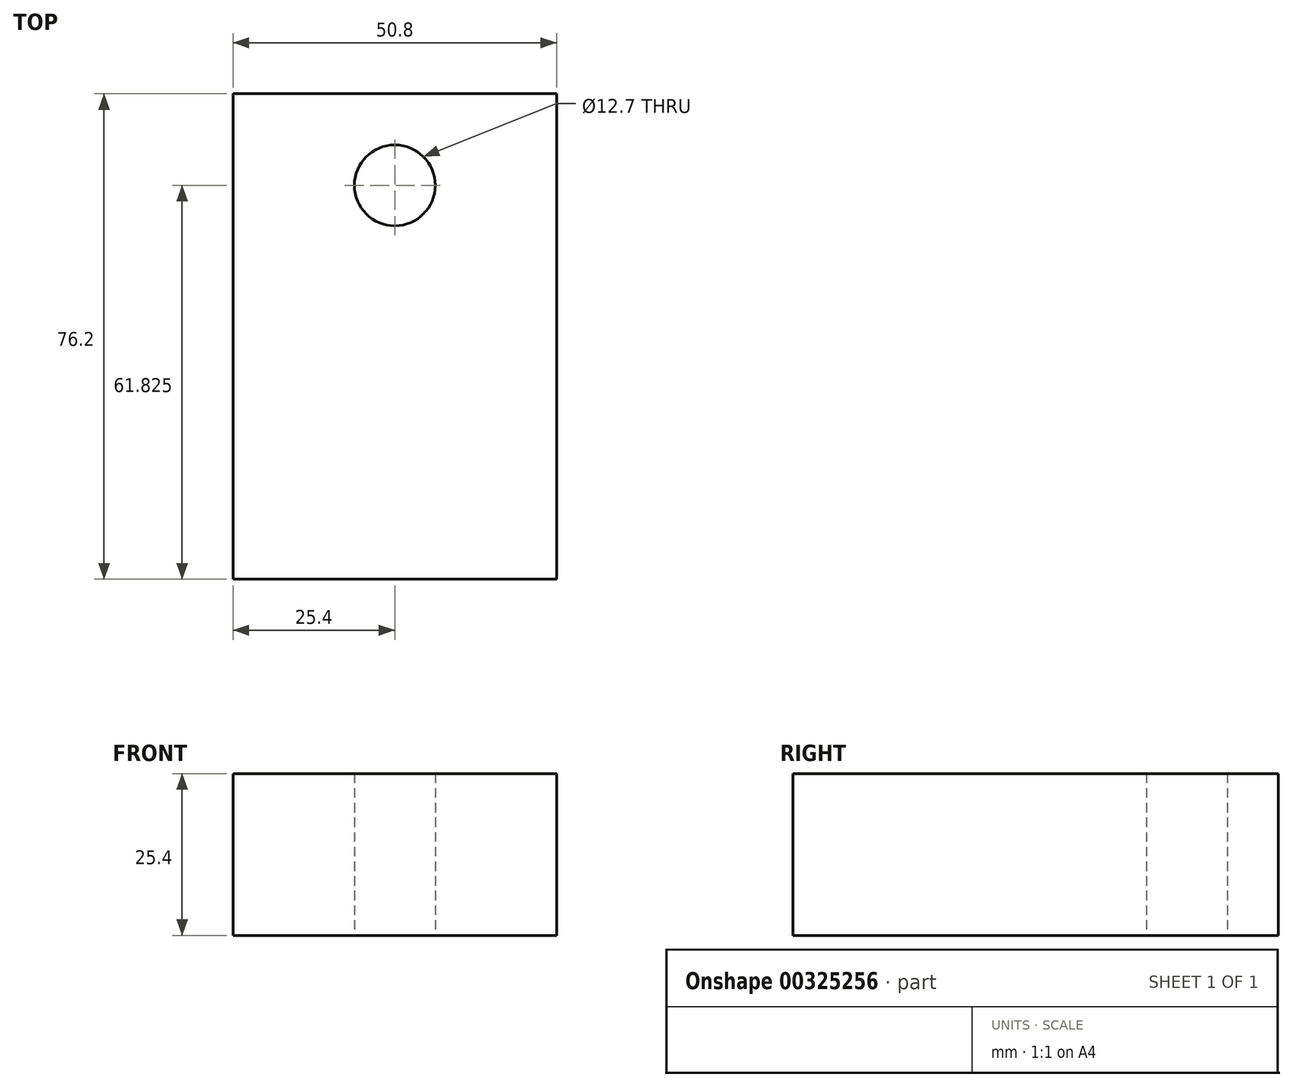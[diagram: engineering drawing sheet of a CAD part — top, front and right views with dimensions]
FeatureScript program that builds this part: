
annotation { "Feature Type Name" : "Feature", "Feature Type Description" : "" }
export const myFeature = defineFeature(function(context is Context, id is Id, definition is map)
    precondition{}
    {
        {
            var Q0;
            Q0=qCreatedBy(makeId("Top.planeOp"),FACE);
            var sketch = newSketch(context, id + "F0", { "sketchPlane" : qUnion([Q0])});
            skLineSegment(sketch, "E0.bottom", {"start": v(25.4, 38.1) * mm, "end": v(-25.4, 38.1) * mm});
            skLineSegment(sketch, "E0.top", {"start": v(25.4, -38.1) * mm, "end": v(-25.4, -38.1) * mm});
            skLineSegment(sketch, "E0.left", {"start": v(25.4, 38.1) * mm, "end": v(25.4, -38.1) * mm});
            skLineSegment(sketch, "E0.right", {"start": v(-25.4, 38.1) * mm, "end": v(-25.4, -38.1) * mm});
            skPoint(sketch, "E0.middle", {"position": v(0, 0) * mm});
            skLineSegment(sketch, "E1", {"start": v(-32.65, 23.72) * mm, "end": v(40.24, 23.72) * mm});
            skCircle(sketch, "E2", {"center": v(0, 23.72) * mm, "radius": 6.35 * mm});
            skPoint(sketch, "E2.centerSnap0", {"position": v(3.8, 23.72) * mm});
            skSolve(sketch);
        }
        {
            var Q0;
            Q0 = qSketchRegion(id + "F0", true);
            extrude(context, id + "F1", {"entities" : qUnion([Q0]), "depth" : 25.4 * mm});
        }
    });
